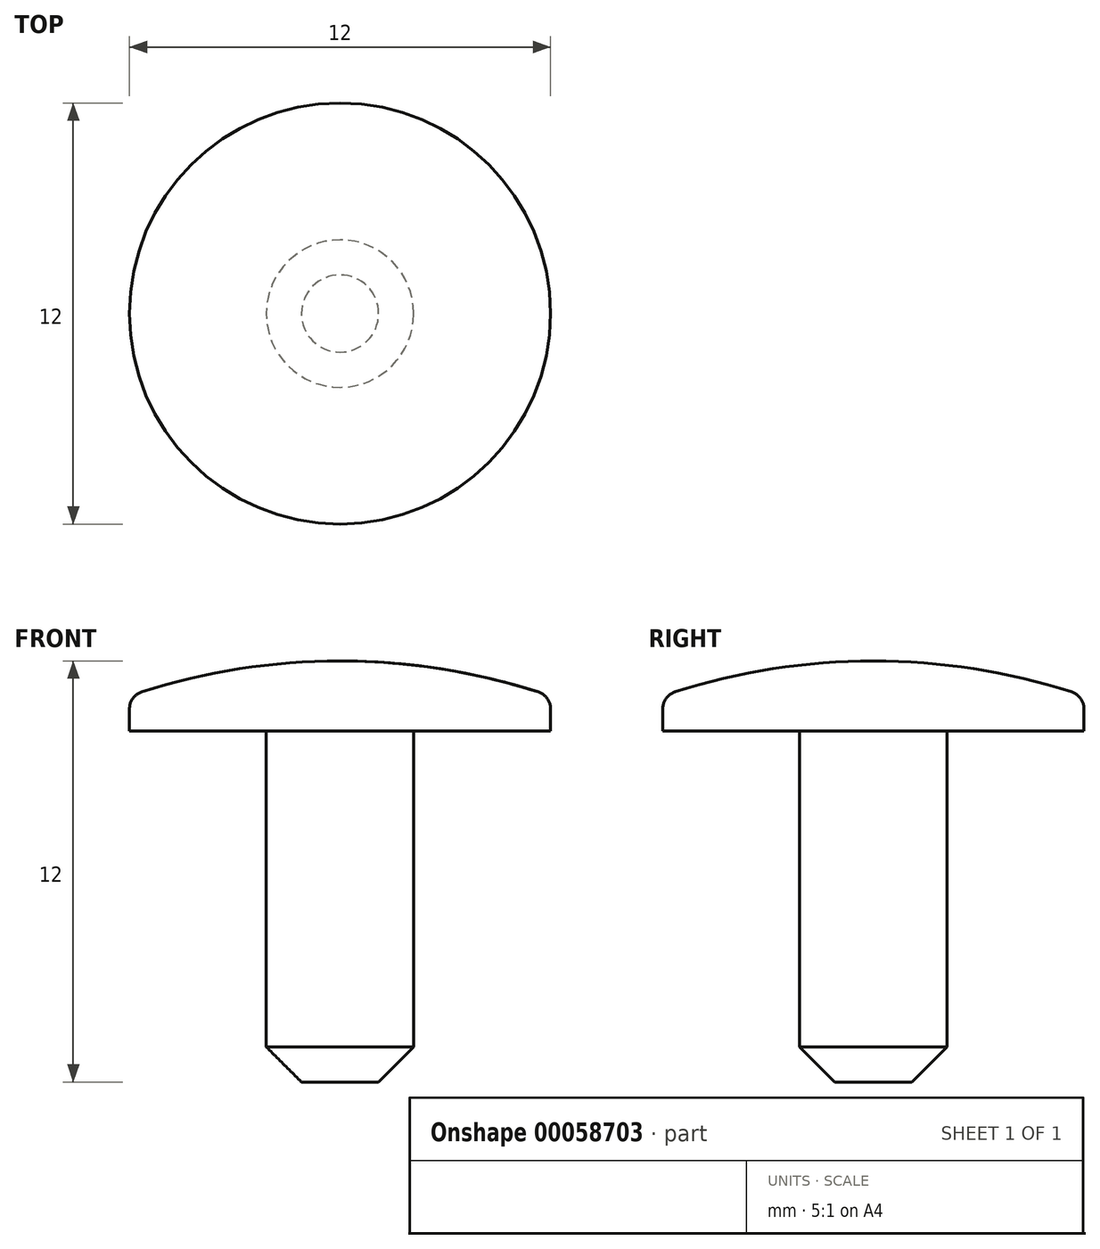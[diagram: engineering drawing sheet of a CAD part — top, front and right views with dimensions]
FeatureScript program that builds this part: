
annotation { "Feature Type Name" : "Feature", "Feature Type Description" : "" }
export const myFeature = defineFeature(function(context is Context, id is Id, definition is map)
    precondition{}
    {
        {
            var Q0;
            Q0=qCreatedBy(makeId("Front.planeOp"),FACE);
            var sketch = newSketch(context, id + "F0", { "sketchPlane" : qUnion([Q0])});
            skLineSegment(sketch, "E0", {"start": v(0, 0) * mm, "end": v(0, 12) * mm});
            skLineSegment(sketch, "E1", {"start": v(0, 0) * mm, "end": v(2.1, 0) * mm});
            skLineSegment(sketch, "E2", {"start": v(2.1, 0) * mm, "end": v(2.1, 10) * mm});
            skLineSegment(sketch, "E3", {"start": v(2.1, 10) * mm, "end": v(6, 10) * mm});
            skLineSegment(sketch, "E4", {"start": v(6, 10) * mm, "end": v(6, 11) * mm});
            skLineSegment(sketch, "E5", {"start": v(0, 0) * mm, "end": v(0, -6.5) * mm, "construction": true});
            skCircle(sketch, "E6", {"center": v(0, -6.5) * mm, "radius": 18.5 * mm, "construction": true});
            skArc(sketch, "E7", {"start": v(6, 11) * mm, "mid": v(3.04, 11.75) * mm, "end": v(0, 12) * mm});
            skSolve(sketch);
        }
        {
            var Q0;
            Q0=makeQuery(id+"F0.imprint","IMPRINT",FACE,{"disambiguationData":[TD([[makeQuery(id+"F0.imprint","IMPRINT",EDGE,{"derivedFrom":sQuery(id+"F0.wireOp",EDGE,"E0")}),-1.0]])]});
            var Q1;
            Q1=sQuery(id+"F0.wireOp",EDGE,"E0");
            revolve(context, id + "F1", {"entities" : qUnion([Q0]), "axis" : qUnion([Q1]), "revolveType" : RevolveType.FULL});
        }
        {
            var Q0;
            Q0=makeQuery(id+"F1.opRevolve","SWEPT_EDGE",EDGE,{"disambiguationData":[OSD([sQuery(id+"F0.wireOp",EDGE,"E1"),sQuery(id+"F0.wireOp",EDGE,"E2")])]});
            chamfer(context, id + "F2", {"entities" : qUnion([Q0]), "width" : 1 * mm, "tangentPropagation" : true});
        }
        {
            var Q0;
            Q0=makeQuery(id+"F1.opRevolve","SWEPT_EDGE",EDGE,{"disambiguationData":[OSD([sQuery(id+"F0.wireOp",EDGE,"E4"),sQuery(id+"F0.wireOp",EDGE,"E7")])]});
            fillet(context, id + "F3", {"entities" : qUnion([Q0]), "radius" : 0.5 * mm, "tangentPropagation" : true, "allowEdgeOverflow" : false});
        }
    });
